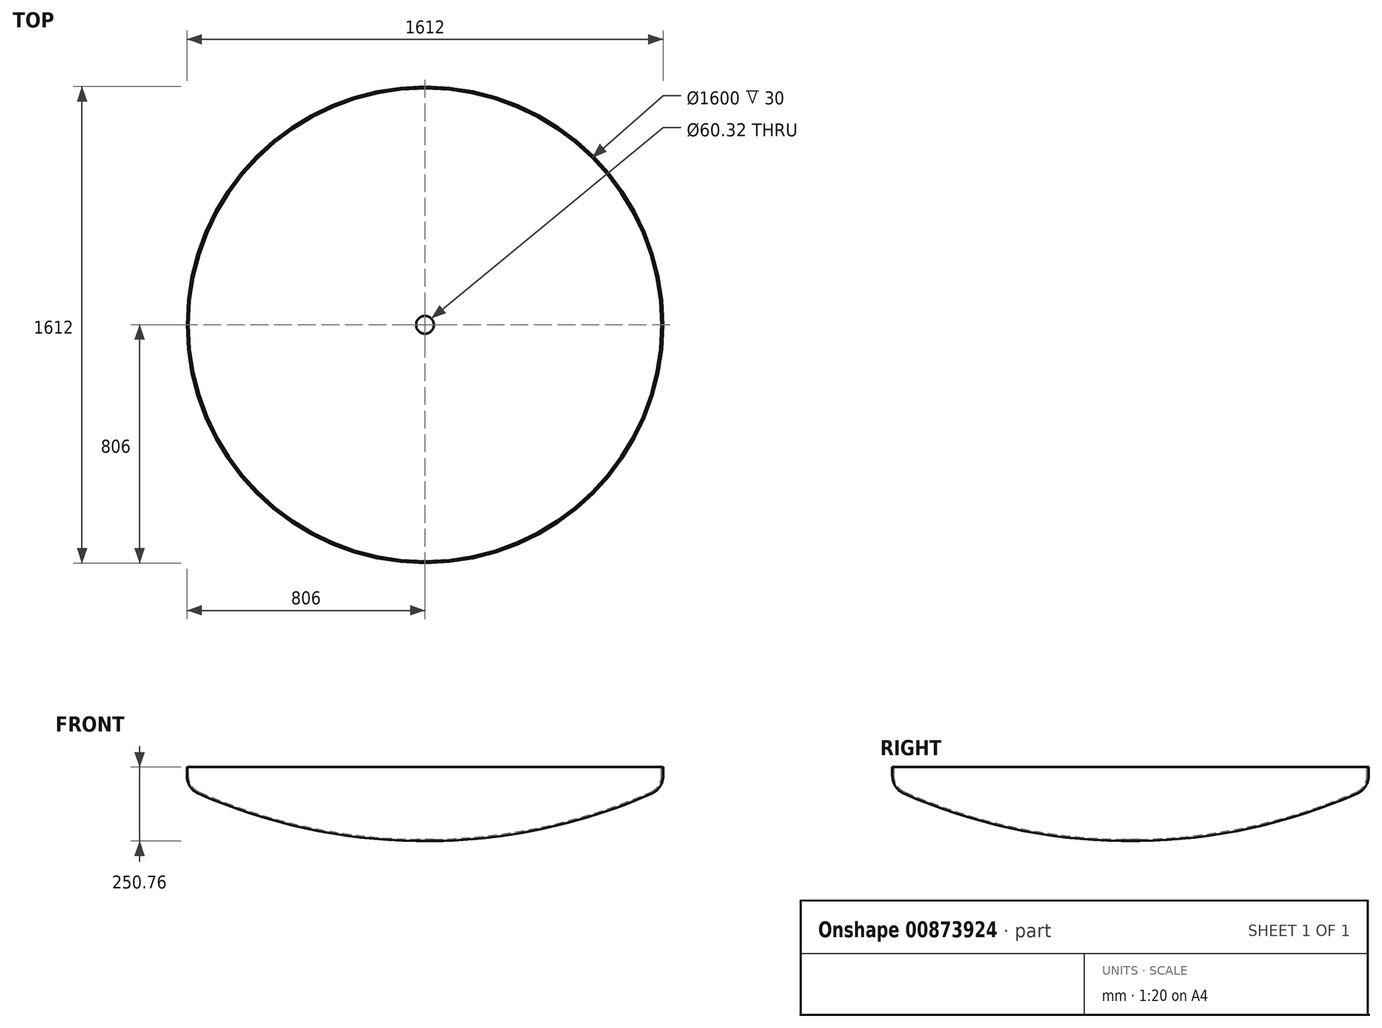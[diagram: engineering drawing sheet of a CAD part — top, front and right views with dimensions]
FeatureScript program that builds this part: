
annotation { "Feature Type Name" : "Feature", "Feature Type Description" : "" }
export const myFeature = defineFeature(function(context is Context, id is Id, definition is map)
    precondition{}
    {
        {
            var Q0;
            Q0=qCreatedBy(makeId("Front.planeOp"),FACE);
            var sketch = newSketch(context, id + "F0", { "sketchPlane" : qUnion([Q0])});
            skLineSegment(sketch, "E0", {"start": v(-800, 0) * mm, "end": v(800, 0) * mm, "construction": true});
            skLineSegment(sketch, "E1", {"start": v(-800, 0) * mm, "end": v(-800, -30) * mm});
            skArc(sketch, "E2", {"start": v(-800, -30) * mm, "mid": v(-790.22, -62.83) * mm, "end": v(-764.08, -84.96) * mm});
            skLineSegment(sketch, "E3", {"start": v(0, 0) * mm, "end": v(0, -245) * mm, "construction": true});
            skArc(sketch, "E4", {"start": v(-764.08, -84.96) * mm, "mid": v(-390.33, -204.56) * mm, "end": v(0, -245) * mm});
            skLineSegment(sketch, "E5.1", {"start": v(-806, 0) * mm, "end": v(-806, -30) * mm});
            skArc(sketch, "E5.2", {"start": v(-806, -30) * mm, "mid": v(-795.25, -66.11) * mm, "end": v(-766.49, -90.45) * mm});
            skArc(sketch, "E5.3", {"start": v(-766.49, -90.45) * mm, "mid": v(-391.56, -210.43) * mm, "end": v(0, -251) * mm});
            skLineSegment(sketch, "E6", {"start": v(-806, 0) * mm, "end": v(-800, 0) * mm});
            skLineSegment(sketch, "E7", {"start": v(0, -245) * mm, "end": v(0, -251) * mm});
            skSolve(sketch);
        }
        {
            var Q0;
            Q0 = qSketchRegion(id + "F0", true);
            var Q1;
            Q1=sQuery(id+"F0.wireOp",EDGE,"E3");
            revolve(context, id + "F1", {"surfaceOperationType" : NewSurfaceOperationType.NEW, "entities" : qUnion([Q0]), "axis" : qUnion([Q1]), "revolveType" : RevolveType.FULL});
        }
        {
            var Q0;
            Q0=qCreatedBy(makeId("Top.planeOp"),FACE);
            var sketch = newSketch(context, id + "F2", { "sketchPlane" : qUnion([Q0])});
            skCircle(sketch, "E8", {"center": v(0, 0) * mm, "radius": 30.16 * mm});
            skSolve(sketch);
        }
        {
            var Q0;
            Q0 = qSketchRegion(id + "F2", true);
            extrude(context, id + "F3", {"entities" : qUnion([Q0]), "operationType" : NewBodyOperationType.REMOVE, "endBound" : BoundingType.THROUGH_ALL, "oppositeDirection" : true, "depth" : 25 * mm, "offsetDistance" : 25 * mm});
        }
    });
